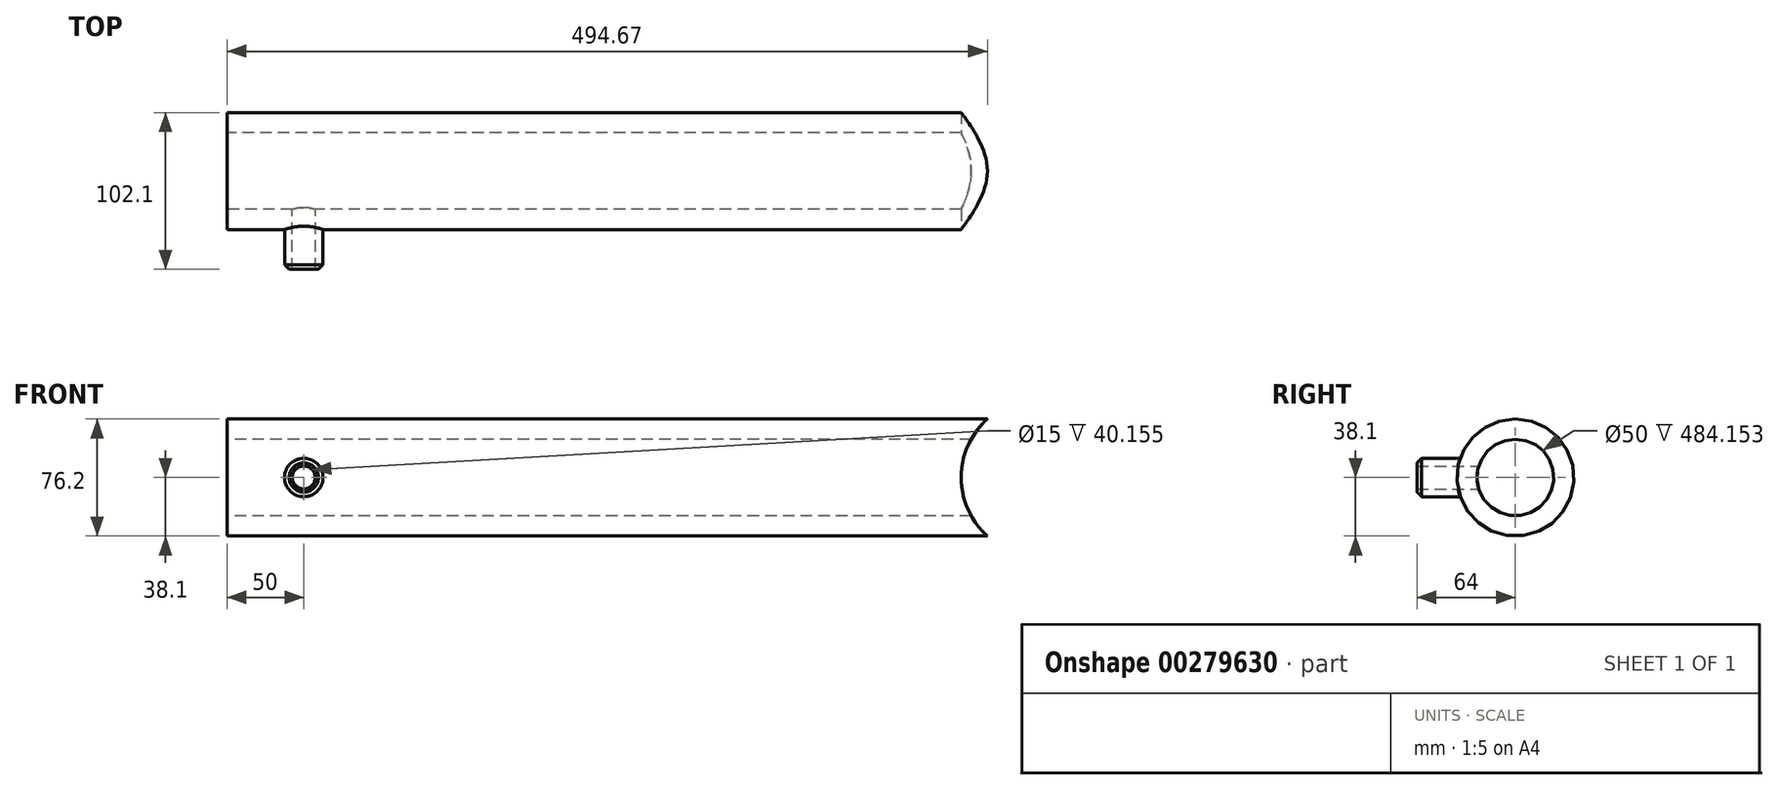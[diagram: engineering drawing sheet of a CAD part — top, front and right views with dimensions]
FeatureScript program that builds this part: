
annotation { "Feature Type Name" : "Feature", "Feature Type Description" : "" }
export const myFeature = defineFeature(function(context is Context, id is Id, definition is map)
    precondition{}
    {
        {
            var Q0;
            Q0=qCreatedBy(makeId("Front.planeOp"),FACE);
            var sketch = newSketch(context, id + "F0", { "sketchPlane" : qUnion([Q0])});
            skCircle(sketch, "E0", {"center": v(0, 0) * mm, "radius": 7.5 * mm});
            skCircle(sketch, "E1", {"center": v(0, 0) * mm, "radius": 12.5 * mm});
            skSolve(sketch);
        }
        {
            var Q0;
            Q0=qSketchRegion(id+"F0",true);
            extrude(context, id + "F1", {"entities" : qUnion([Q0]), "depth" : 64 * mm});
        }
        {
            var Q0;
            Q0=qCreatedBy(makeId("Right.planeOp"),FACE);
            var sketch = newSketch(context, id + "F2", { "sketchPlane" : qUnion([Q0])});
            skCircle(sketch, "E2", {"center": v(0, 0) * mm, "radius": 38.1 * mm});
            skCircle(sketch, "E3", {"center": v(0, 0) * mm, "radius": 25 * mm});
            skSolve(sketch);
        }
        {
            var Q0;
            Q0=qSketchRegion(id+"F2",true);
            extrude(context, id + "F3", {"entities" : qUnion([Q0]), "operationType" : NewBodyOperationType.ADD, "depth" : 100 * mm});
        }
        {
            var Q0;
            Q0=qSketchRegion(id+"F2",true);
            extrude(context, id + "F4", {"entities" : qUnion([Q0]), "operationType" : NewBodyOperationType.ADD, "oppositeDirection" : true, "depth" : 50 * mm});
        }
        {
            var Q0;
            Q0=makeQuery(id+"F1.opExtrude","CAP_EDGE",EDGE,{"disambiguationData":[OSD([sQuery(id+"F0.wireOp",EDGE,"E1")])],"isStart":false});
            chamfer(context, id + "F5", {"entities" : qUnion([Q0]), "width" : 3 * mm, "tangentPropagation" : true});
        }
        {
            var Q0;
            Q0=makeQuery(id+"F4.opExtrude","CAP_FACE",FACE,{"disambiguationData":[OSD([sQuery(id+"F2.wireOp",EDGE,"E2"),sQuery(id+"F2.wireOp",EDGE,"E3")])],"isStart":false});
            var sketch = newSketch(context, id + "F6", { "sketchPlane" : qUnion([Q0])});
            skCircle(sketch, "E4", {"center": v(0, 0) * mm, "radius": 25 * mm});
            skSolve(sketch);
        }
        {
            var Q0;
            Q0=qSketchRegion(id+"F6",true);
            extrude(context, id + "F7", {"entities" : qUnion([Q0]), "operationType" : NewBodyOperationType.REMOVE, "oppositeDirection" : true, "depth" : 200 * mm});
        }
        {
            var Q0;
            Q0=makeQuery(id+"F1.opExtrude","CAP_FACE",FACE,{"disambiguationData":[OSD([sQuery(id+"F0.wireOp",EDGE,"E0"),sQuery(id+"F0.wireOp",EDGE,"E1")])],"isStart":false});
            var sketch = newSketch(context, id + "F8", { "sketchPlane" : qUnion([Q0])});
            skCircle(sketch, "E5", {"center": v(0, 0) * mm, "radius": 7.5 * mm});
            skSolve(sketch);
        }
        {
            var Q0;
            Q0=qSketchRegion(id+"F8",true);
            extrude(context, id + "F9", {"entities" : qUnion([Q0]), "operationType" : NewBodyOperationType.REMOVE, "oppositeDirection" : true, "depth" : 50 * mm});
        }
        {
            var Q0;
            Q0=makeQuery(id+"F3.opExtrude","CAP_FACE",FACE,{"disambiguationData":[OSD([sQuery(id+"F2.wireOp",EDGE,"E2"),sQuery(id+"F2.wireOp",EDGE,"E3")])],"isStart":false});
            extrude(context, id + "F10", {"entities" : qUnion([Q0]), "operationType" : NewBodyOperationType.ADD, "depth" : 100 * mm});
        }
        {
            var Q0;
            Q0=makeQuery(id+"F1.opExtrude","CAP_FACE",FACE,{"disambiguationData":[OSD([sQuery(id+"F0.wireOp",EDGE,"E0"),sQuery(id+"F0.wireOp",EDGE,"E1")])],"isStart":false});
            var sketch = newSketch(context, id + "F11", { "sketchPlane" : qUnion([Q0])});
            skCircle(sketch, "E6", {"center": v(0, 0) * mm, "radius": 7.5 * mm});
            skSolve(sketch);
        }
        {
            var Q0;
            Q0=qSketchRegion(id+"F11",true);
            extrude(context, id + "F12", {"entities" : qUnion([Q0]), "operationType" : NewBodyOperationType.REMOVE, "oppositeDirection" : true, "depth" : 50 * mm});
        }
        {
            var Q0;
            Q0=makeQuery(id+"F10.opExtrude","CAP_FACE",FACE,{"disambiguationData":[OSD([sQuery(id+"F2.wireOp",EDGE,"E2"),sQuery(id+"F2.wireOp",EDGE,"E3")])],"isStart":false});
            extrude(context, id + "F13", {"entities" : qUnion([Q0]), "operationType" : NewBodyOperationType.ADD, "depth" : 250 * mm});
        }
        {
            var Q0;
            Q0=qCreatedBy(makeId("Top.planeOp"),FACE);
            var sketch = newSketch(context, id + "F14", { "sketchPlane" : qUnion([Q0])});
            skLineSegment(sketch, "E7", {"start": v(478.7, 52.96) * mm, "end": v(478.7, -52.1) * mm, "construction": true});
            skLineSegment(sketch, "E8", {"start": v(427.61, 51.93) * mm, "end": v(427.61, -50.66) * mm});
            skLineSegment(sketch, "E9", {"start": v(427.61, -50.66) * mm, "end": v(478.7, -52.1) * mm});
            skLineSegment(sketch, "E10", {"start": v(427.61, 51.93) * mm, "end": v(478.7, 52.96) * mm});
            skLineSegment(sketch, "E11", {"start": v(455.14, -51.43) * mm, "end": v(455.14, 52.96) * mm});
            skSolve(sketch);
        }
        {
            var Q0;
            {var subQ0=sQuery(id+"F14.wireOp",EDGE,"E8");Q0=makeQuery(id+"F14.imprint","IMPRINT",FACE,{"disambiguationData":[TD([[makeQuery(id+"F14.imprint","IMPRINT",EDGE,{"derivedFrom":subQ0}),1.0]])]});}
            var Q1;
            Q1=sQuery(id+"F14.wireOp",EDGE,"E7");
            revolve(context, id + "F15", {"operationType" : NewBodyOperationType.REMOVE, "entities" : qUnion([Q0]), "axis" : qUnion([Q1]), "revolveType" : RevolveType.FULL, "oppositeDirection" : true});
        }
    });
